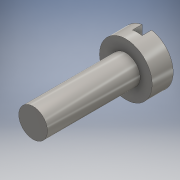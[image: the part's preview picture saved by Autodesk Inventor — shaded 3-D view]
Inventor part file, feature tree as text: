
AUTODESK INVENTOR PART (.ipt)
format: ipt  version: 2016 (Build 200138000, 138)  size: 129,024 bytes
history: native  units: mm
features: extrude x3, sketch x3
ambient origin geometry x8: Origin, YZ Plane, XZ Plane, XY Plane, X Axis, Y Axis, Z Axis, Center Point
bodies: Solid1 (feature_tree)
feature tree (6):
  extrude  "Extrusion1"  Depth=9.7mm TaperAngle=0.0deg
  extrude  "Extrusion2"  Depth=2.2mm TaperAngle=0.0deg
  extrude  "Extrusion3"  Depth=1.0mm TaperAngle=0.0deg
  sketch  "Sketch1"  dims[d0=3.0mm d1=9.7mm d2=0.0mm]
  sketch  "Sketch2"  dims[d3=5.5mm d4=2.2mm d5=0.0mm]
  sketch  "Sketch3"  dims[d6=1.0mm d7=1.0mm d8=0.0mm]
